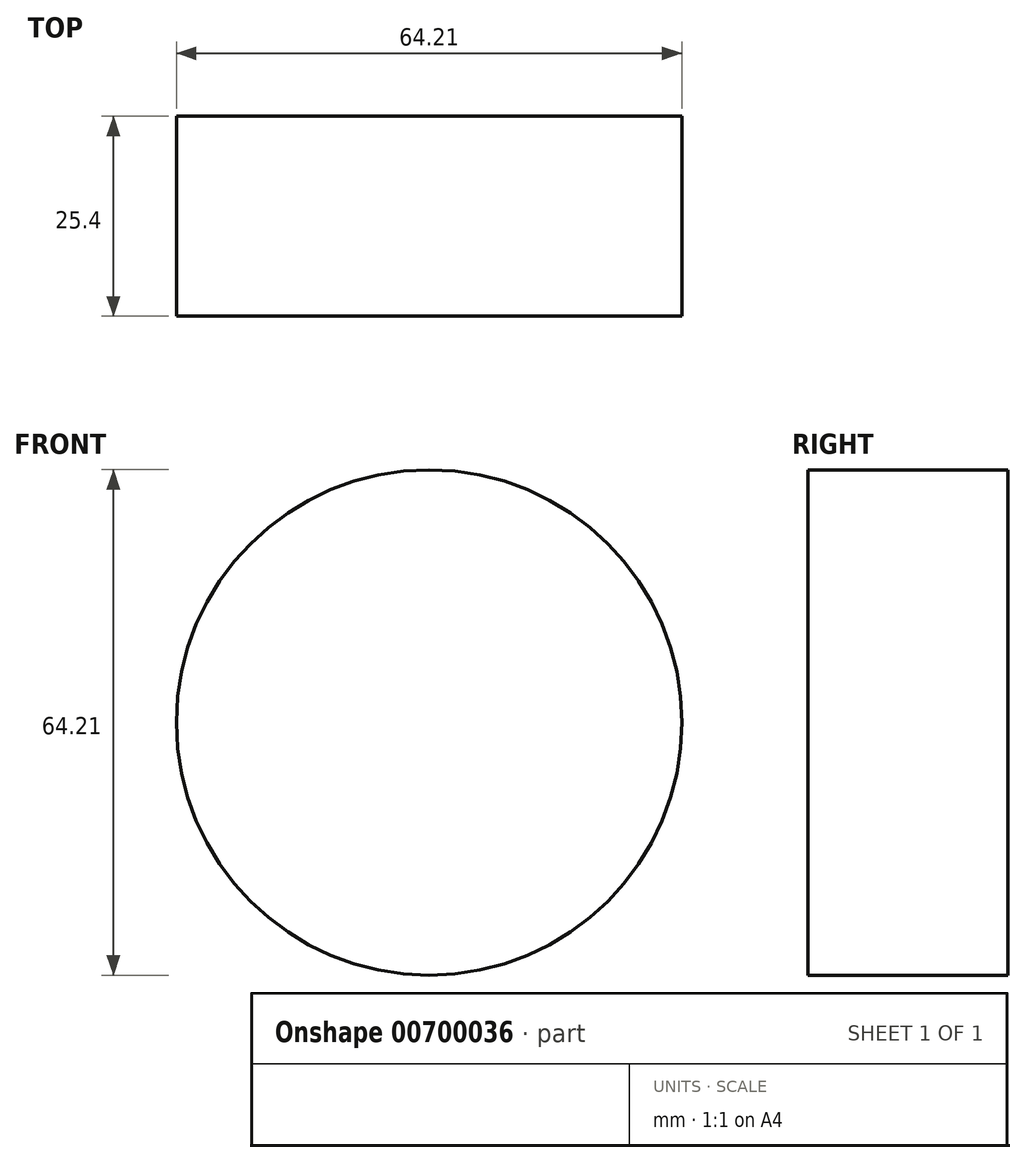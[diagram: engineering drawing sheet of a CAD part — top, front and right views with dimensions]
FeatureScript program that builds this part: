
annotation { "Feature Type Name" : "Feature", "Feature Type Description" : "" }
export const myFeature = defineFeature(function(context is Context, id is Id, definition is map)
    precondition{}
    {
        {
            var Q0;
            Q0=qCreatedBy(makeId("Front.planeOp"),FACE);
            var sketch = newSketch(context, id + "F0", { "sketchPlane" : qUnion([Q0])});
            skCircle(sketch, "E0", {"center": v(-42.81, 24.46) * mm, "radius": 32.1 * mm});
            skSolve(sketch);
        }
        {
            var Q0;
            Q0 = qSketchRegion(id + "F0", true);
            extrude(context, id + "F1", {"entities" : qUnion([Q0]), "depth" : 25.4 * mm, "offsetDistance" : 25.4 * mm});
        }
    });
